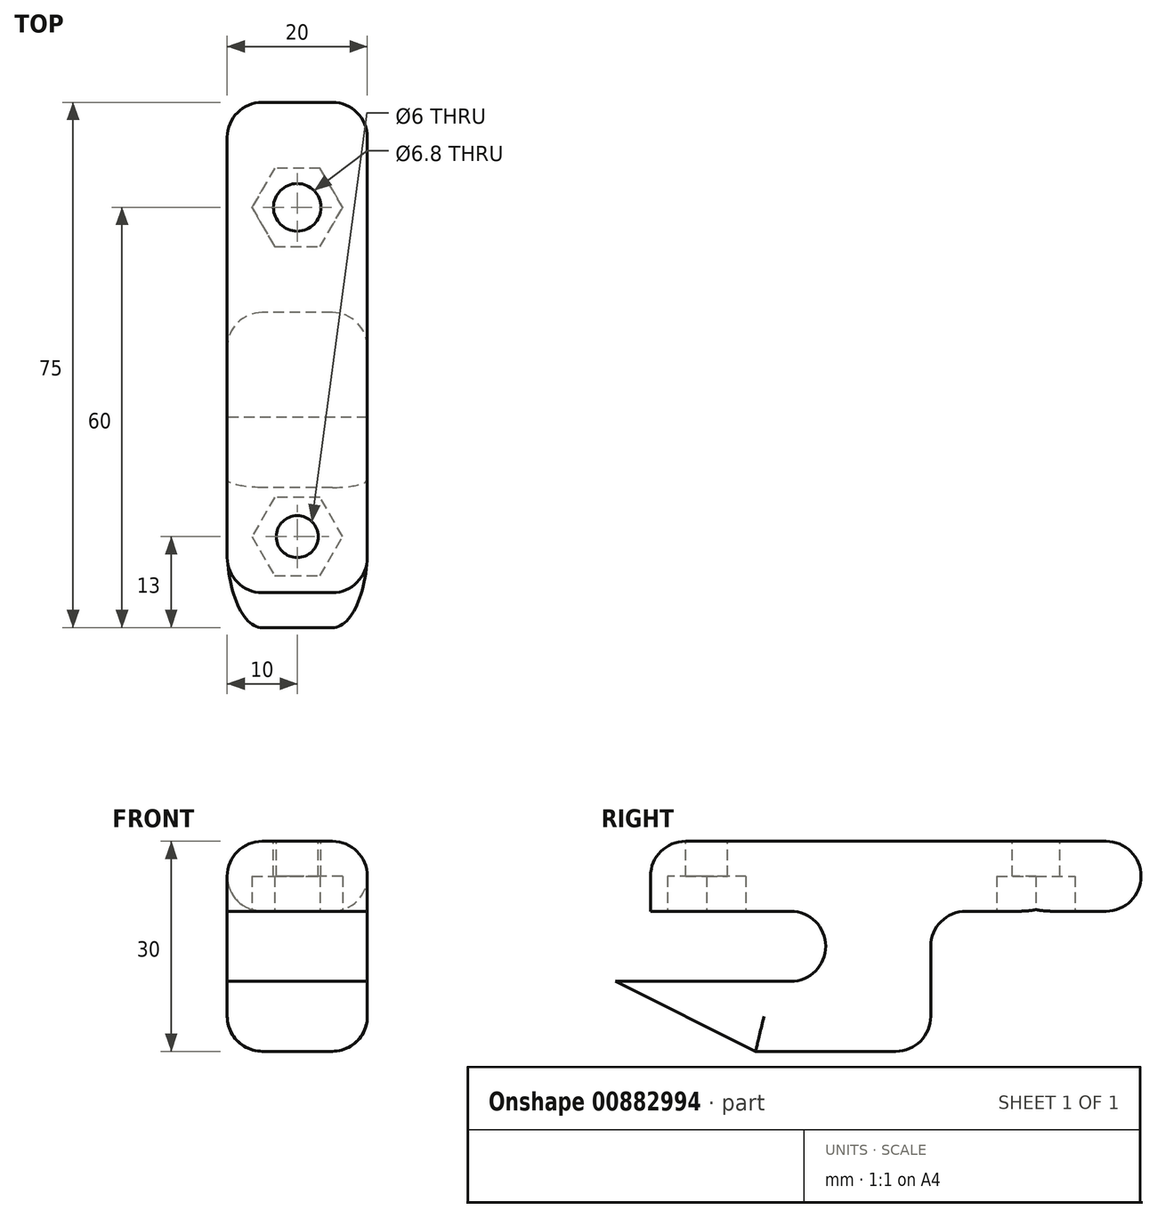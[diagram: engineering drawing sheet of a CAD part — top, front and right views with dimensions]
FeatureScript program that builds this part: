
annotation { "Feature Type Name" : "Feature", "Feature Type Description" : "" }
export const myFeature = defineFeature(function(context is Context, id is Id, definition is map)
    precondition{}
    {
        {
            var Q0;
            Q0=qCreatedBy(makeId("Right.planeOp"),FACE);
            var sketch = newSketch(context, id + "F0", { "sketchPlane" : qUnion([Q0])});
            skLineSegment(sketch, "E0.bottom", {"start": v(7.5, -5) * mm, "end": v(-7.5, -5) * mm});
            skLineSegment(sketch, "E0.top", {"start": v(7.5, 5) * mm, "end": v(-7.5, 5) * mm});
            skLineSegment(sketch, "E0.left", {"start": v(7.5, -5) * mm, "end": v(7.5, 5) * mm});
            skLineSegment(sketch, "E0.right", {"start": v(-7.5, -5) * mm, "end": v(-7.5, 5) * mm});
            skPoint(sketch, "E0.middle", {"position": v(0, 0) * mm});
            skLineSegment(sketch, "E1.bottom", {"start": v(7.5, 5) * mm, "end": v(-32.5, 5) * mm});
            skLineSegment(sketch, "E1.top", {"start": v(7.5, 15) * mm, "end": v(-32.5, 15) * mm});
            skLineSegment(sketch, "E1.left", {"start": v(7.5, 5) * mm, "end": v(7.5, 15) * mm});
            skLineSegment(sketch, "E1.right", {"start": v(-32.5, 5) * mm, "end": v(-32.5, 15) * mm});
            skLineSegment(sketch, "E2.bottom", {"start": v(7.5, -5) * mm, "end": v(-37.5, -5) * mm});
            skLineSegment(sketch, "E2.top", {"start": v(7.5, -15) * mm, "end": v(-37.5, -15) * mm});
            skLineSegment(sketch, "E2.left", {"start": v(7.5, -5) * mm, "end": v(7.5, -15) * mm});
            skLineSegment(sketch, "E2.right", {"start": v(-37.5, -5) * mm, "end": v(-37.5, -15) * mm});
            skLineSegment(sketch, "E3.bottom", {"start": v(7.5, 5) * mm, "end": v(37.5, 5) * mm});
            skLineSegment(sketch, "E3.top", {"start": v(7.5, 15) * mm, "end": v(37.5, 15) * mm});
            skLineSegment(sketch, "E3.right", {"start": v(37.5, 5) * mm, "end": v(37.5, 15) * mm});
            skSolve(sketch);
        }
        {
            var Q0;
            {var subQ0=makeQuery(id+"F0.imprint","IMPRINT",EDGE,{"derivedFrom":sQuery(id+"F0.wireOp",EDGE,"E1.left")});var subQ1=makeQuery(id+"F0.imprint","IMPRINT",EDGE,{"derivedFrom":sQuery(id+"F0.wireOp",EDGE,"E0.top")});var subQ2=makeQuery(id+"F0.imprint","IMPRINT",EDGE,{"derivedFrom":sQuery(id+"F0.wireOp",EDGE,"E0.bottom")});Q0=qUnion([makeQuery(id+"F0.imprint","IMPRINT",FACE,{"disambiguationData":[TD([[subQ2,1.0]])]}),makeQuery(id+"F0.imprint","IMPRINT",FACE,{"disambiguationData":[TD([[subQ0,-1.0]])]}),makeQuery(id+"F0.imprint","IMPRINT",FACE,{"disambiguationData":[TD([[subQ2,-1.0]])]}),makeQuery(id+"F0.imprint","IMPRINT",FACE,{"disambiguationData":[TD([[subQ1,-1.0]])]})]);}
            extrude(context, id + "F1", {"entities" : qUnion([Q0]), "depth" : 20 * mm, "offsetDistance" : 25 * mm});
        }
        {
            var Q0;
            Q0=makeQuery(id+"F1.opExtrude","SWEPT_FACE",FACE,{"disambiguationData":[OSD([sQuery(id+"F0.wireOp",EDGE,"E1.top"),sQuery(id+"F0.wireOp",EDGE,"E3.top")])]});
            var sketch = newSketch(context, id + "F2", { "sketchPlane" : qUnion([Q0])});
            skCircle(sketch, "E4", {"center": v(10, 22.5) * mm, "radius": 3.4 * mm});
            skCircle(sketch, "E5", {"center": v(10, -24.5) * mm, "radius": 3 * mm});
            skSolve(sketch);
        }
        {
            var Q0;
            Q0=makeQuery(id+"F2.imprint","IMPRINT",FACE,{"disambiguationData":[TD([[makeQuery(id+"F2.imprint","IMPRINT",EDGE,{"derivedFrom":sQuery(id+"F2.wireOp",EDGE,"E5")}),1.0]])]});
            var Q1;
            Q1=makeQuery(id+"F2.imprint","IMPRINT",FACE,{"disambiguationData":[TD([[makeQuery(id+"F2.imprint","IMPRINT",EDGE,{"derivedFrom":sQuery(id+"F2.wireOp",EDGE,"E4")}),1.0]])]});
            extrude(context, id + "F3", {"entities" : qUnion([Q0, Q1]), "operationType" : NewBodyOperationType.REMOVE, "endBound" : BoundingType.UP_TO_NEXT, "oppositeDirection" : true, "depth" : 25 * mm, "offsetDistance" : 25 * mm});
        }
        {
            var Q0;
            Q0=makeQuery(id+"F1.opExtrude","SWEPT_FACE",FACE,{"disambiguationData":[OSD([sQuery(id+"F0.wireOp",EDGE,"E3.bottom")])]});
            var sketch = newSketch(context, id + "F4", { "sketchPlane" : qUnion([Q0])});
            skCircle(sketch, "E6.cCircle", {"center": v(10, -22.5) * mm, "radius": 5.6 * mm, "construction": true});
            skLineSegment(sketch, "E6.0", {"start": v(13.23, -28.1) * mm, "end": v(6.77, -28.1) * mm});
            skLineSegment(sketch, "E6.1", {"start": v(6.77, -28.1) * mm, "end": v(3.53, -22.5) * mm});
            skLineSegment(sketch, "E6.2", {"start": v(3.53, -22.5) * mm, "end": v(6.77, -16.9) * mm});
            skLineSegment(sketch, "E6.3", {"start": v(6.77, -16.9) * mm, "end": v(13.23, -16.9) * mm});
            skLineSegment(sketch, "E6.4", {"start": v(13.23, -16.9) * mm, "end": v(16.47, -22.5) * mm});
            skLineSegment(sketch, "E6.5", {"start": v(16.47, -22.5) * mm, "end": v(13.23, -28.1) * mm});
            skPoint(sketch, "E6.0.midPoint", {"position": v(10, -28.1) * mm});
            skSolve(sketch);
        }
        {
            var Q0;
            Q0 = qSketchRegion(id + "F4", true);
            extrude(context, id + "F5", {"entities" : qUnion([Q0]), "operationType" : NewBodyOperationType.REMOVE, "oppositeDirection" : true, "depth" : 5 * mm, "offsetDistance" : 25 * mm});
        }
        {
            var Q0;
            Q0=makeQuery(id+"F1.opExtrude","SWEPT_EDGE",EDGE,{"disambiguationData":[OSD([sQuery(id+"F0.wireOp",EDGE,"E2.top"),sQuery(id+"F0.wireOp",EDGE,"E2.right")])]});
            chamfer(context, id + "F6", {"entities" : qUnion([Q0]), "chamferType" : ChamferType.TWO_OFFSETS, "width1" : 20 * mm, "oppositeDirection" : false, "width2" : 10 * mm, "tangentPropagation" : true});
        }
        {
            var Q0;
            Q0=makeQuery(id+"F1.opExtrude","CAP_EDGE",EDGE,{"disambiguationData":[OSD([sQuery(id+"F0.wireOp",EDGE,"E3.right")])],"isStart":true});
            var Q1;
            Q1=makeQuery(id+"F1.opExtrude","CAP_EDGE",EDGE,{"disambiguationData":[OSD([sQuery(id+"F0.wireOp",EDGE,"E3.right")])],"isStart":false});
            var Q2;
            Q2=makeQuery(id+"F1.opExtrude","CAP_EDGE",EDGE,{"disambiguationData":[OSD([sQuery(id+"F0.wireOp",EDGE,"E0.left"),sQuery(id+"F0.wireOp",EDGE,"E2.left")])],"isStart":false});
            var Q3;
            Q3=makeQuery(id+"F1.opExtrude","CAP_EDGE",EDGE,{"disambiguationData":[OSD([sQuery(id+"F0.wireOp",EDGE,"E0.left"),sQuery(id+"F0.wireOp",EDGE,"E2.left")])],"isStart":true});
            var Q4;
            Q4=makeQuery(id+"F1.opExtrude","SWEPT_EDGE",EDGE,{"disambiguationData":[OSD([sQuery(id+"F0.wireOp",EDGE,"E2.top"),sQuery(id+"F0.wireOp",EDGE,"E2.left")])]});
            var Q5;
            Q5=makeQuery(id+"F1.opExtrude","CAP_EDGE",EDGE,{"disambiguationData":[OSD([sQuery(id+"F0.wireOp",EDGE,"E2.top")])],"isStart":false});
            var Q6;
            Q6=makeQuery(id+"F1.opExtrude","CAP_EDGE",EDGE,{"disambiguationData":[OSD([sQuery(id+"F0.wireOp",EDGE,"E2.top")])],"isStart":true});
            var Q7;
            {var subQ0=sQuery(id+"F0.wireOp",EDGE,"E2.right");var subQ1=sQuery(id+"F0.wireOp",EDGE,"E2.top");Q7=makeQuery(id+"F6.opChamfer","BLEND_EDGE",EDGE,{"blendedFrom":[makeQuery(id+"F1.opExtrude","SWEPT_EDGE",EDGE,{"disambiguationData":[OSD([subQ1,subQ0])]}),makeQuery(id+"F1.opExtrude","CAP_FACE",FACE,{"disambiguationData":[OSD([sQuery(id+"F0.wireOp",EDGE,"E0.left"),sQuery(id+"F0.wireOp",EDGE,"E0.right"),sQuery(id+"F0.wireOp",EDGE,"E1.bottom"),sQuery(id+"F0.wireOp",EDGE,"E1.top"),sQuery(id+"F0.wireOp",EDGE,"E1.right"),sQuery(id+"F0.wireOp",EDGE,"E2.bottom"),subQ1,sQuery(id+"F0.wireOp",EDGE,"E2.left"),subQ0,sQuery(id+"F0.wireOp",EDGE,"E3.bottom"),sQuery(id+"F0.wireOp",EDGE,"E3.top"),sQuery(id+"F0.wireOp",EDGE,"E3.right")])],"isStart":true})],"blendedInto":[makeQuery(id+"F1.opExtrude","CAP_FACE",FACE,{"disambiguationData":[OSD([sQuery(id+"F0.wireOp",EDGE,"E0.left"),sQuery(id+"F0.wireOp",EDGE,"E0.right"),sQuery(id+"F0.wireOp",EDGE,"E1.bottom"),sQuery(id+"F0.wireOp",EDGE,"E1.top"),sQuery(id+"F0.wireOp",EDGE,"E1.right"),sQuery(id+"F0.wireOp",EDGE,"E2.bottom"),subQ1,sQuery(id+"F0.wireOp",EDGE,"E2.left"),subQ0,sQuery(id+"F0.wireOp",EDGE,"E3.bottom"),sQuery(id+"F0.wireOp",EDGE,"E3.top"),sQuery(id+"F0.wireOp",EDGE,"E3.right")])],"isStart":true})]});}
            var Q8;
            {var subQ0=sQuery(id+"F0.wireOp",EDGE,"E2.right");var subQ1=sQuery(id+"F0.wireOp",EDGE,"E2.top");Q8=makeQuery(id+"F6.opChamfer","BLEND_EDGE",EDGE,{"blendedFrom":[makeQuery(id+"F1.opExtrude","SWEPT_EDGE",EDGE,{"disambiguationData":[OSD([subQ1,subQ0])]}),makeQuery(id+"F1.opExtrude","CAP_FACE",FACE,{"disambiguationData":[OSD([sQuery(id+"F0.wireOp",EDGE,"E0.left"),sQuery(id+"F0.wireOp",EDGE,"E0.right"),sQuery(id+"F0.wireOp",EDGE,"E1.bottom"),sQuery(id+"F0.wireOp",EDGE,"E1.top"),sQuery(id+"F0.wireOp",EDGE,"E1.right"),sQuery(id+"F0.wireOp",EDGE,"E2.bottom"),subQ1,sQuery(id+"F0.wireOp",EDGE,"E2.left"),subQ0,sQuery(id+"F0.wireOp",EDGE,"E3.bottom"),sQuery(id+"F0.wireOp",EDGE,"E3.top"),sQuery(id+"F0.wireOp",EDGE,"E3.right")])],"isStart":false})],"blendedInto":[makeQuery(id+"F1.opExtrude","CAP_FACE",FACE,{"disambiguationData":[OSD([sQuery(id+"F0.wireOp",EDGE,"E0.left"),sQuery(id+"F0.wireOp",EDGE,"E0.right"),sQuery(id+"F0.wireOp",EDGE,"E1.bottom"),sQuery(id+"F0.wireOp",EDGE,"E1.top"),sQuery(id+"F0.wireOp",EDGE,"E1.right"),sQuery(id+"F0.wireOp",EDGE,"E2.bottom"),subQ1,sQuery(id+"F0.wireOp",EDGE,"E2.left"),subQ0,sQuery(id+"F0.wireOp",EDGE,"E3.bottom"),sQuery(id+"F0.wireOp",EDGE,"E3.top"),sQuery(id+"F0.wireOp",EDGE,"E3.right")])],"isStart":false})]});}
            var Q9;
            Q9=makeQuery(id+"F1.opExtrude","CAP_EDGE",EDGE,{"disambiguationData":[OSD([sQuery(id+"F0.wireOp",EDGE,"E3.bottom")])],"isStart":false});
            var Q10;
            Q10=makeQuery(id+"F1.opExtrude","CAP_EDGE",EDGE,{"disambiguationData":[OSD([sQuery(id+"F0.wireOp",EDGE,"E3.bottom")])],"isStart":true});
            var Q11;
            Q11=makeQuery(id+"F1.opExtrude","CAP_EDGE",EDGE,{"disambiguationData":[OSD([sQuery(id+"F0.wireOp",EDGE,"E1.top"),sQuery(id+"F0.wireOp",EDGE,"E3.top")])],"isStart":true});
            var Q12;
            Q12=makeQuery(id+"F1.opExtrude","CAP_EDGE",EDGE,{"disambiguationData":[OSD([sQuery(id+"F0.wireOp",EDGE,"E1.top"),sQuery(id+"F0.wireOp",EDGE,"E3.top")])],"isStart":false});
            var Q13;
            Q13=makeQuery(id+"F1.opExtrude","CAP_EDGE",EDGE,{"disambiguationData":[OSD([sQuery(id+"F0.wireOp",EDGE,"E1.right")])],"isStart":false});
            var Q14;
            Q14=makeQuery(id+"F1.opExtrude","CAP_EDGE",EDGE,{"disambiguationData":[OSD([sQuery(id+"F0.wireOp",EDGE,"E1.right")])],"isStart":true});
            var Q15;
            Q15=makeQuery(id+"F1.opExtrude","SWEPT_EDGE",EDGE,{"disambiguationData":[OSD([sQuery(id+"F0.wireOp",EDGE,"E1.top"),sQuery(id+"F0.wireOp",EDGE,"E1.right")])]});
            var Q16;
            Q16=makeQuery(id+"F1.opExtrude","SWEPT_EDGE",EDGE,{"disambiguationData":[OSD([sQuery(id+"F0.wireOp",EDGE,"E3.top"),sQuery(id+"F0.wireOp",EDGE,"E3.right")])]});
            var Q17;
            Q17=makeQuery(id+"F1.opExtrude","SWEPT_EDGE",EDGE,{"disambiguationData":[OSD([sQuery(id+"F0.wireOp",EDGE,"E3.bottom"),sQuery(id+"F0.wireOp",EDGE,"E3.right")])]});
            var Q18;
            Q18=makeQuery(id+"F1.opExtrude","SWEPT_EDGE",EDGE,{"disambiguationData":[OSD([sQuery(id+"F0.wireOp",EDGE,"E0.top"),sQuery(id+"F0.wireOp",EDGE,"E0.left"),sQuery(id+"F0.wireOp",EDGE,"E1.left"),sQuery(id+"F0.wireOp",EDGE,"E3.bottom")])]});
            var Q19;
            Q19=makeQuery(id+"F1.opExtrude","SWEPT_EDGE",EDGE,{"disambiguationData":[OSD([sQuery(id+"F0.wireOp",EDGE,"E0.bottom"),sQuery(id+"F0.wireOp",EDGE,"E0.right"),sQuery(id+"F0.wireOp",EDGE,"E2.bottom")])]});
            var Q20;
            Q20=makeQuery(id+"F1.opExtrude","SWEPT_EDGE",EDGE,{"disambiguationData":[OSD([sQuery(id+"F0.wireOp",EDGE,"E0.top"),sQuery(id+"F0.wireOp",EDGE,"E0.right"),sQuery(id+"F0.wireOp",EDGE,"E1.bottom")])]});
            fillet(context, id + "F7", {"entities" : qUnion([Q0, Q1, Q2, Q3, Q4, Q5, Q6, Q7, Q8, Q9, Q10, Q11, Q12, Q13, Q14, Q15, Q16, Q17, Q18, Q19, Q20]), "radius" : 5 * mm, "tangentPropagation" : true, "allowEdgeOverflow" : false});
        }
        {
            var Q0;
            Q0=makeQuery(id+"F1.opExtrude","SWEPT_FACE",FACE,{"disambiguationData":[OSD([sQuery(id+"F0.wireOp",EDGE,"E1.bottom")])]});
            var sketch = newSketch(context, id + "F8", { "sketchPlane" : qUnion([Q0])});
            skCircle(sketch, "E7.cCircle", {"center": v(10, 24.5) * mm, "radius": 5.6 * mm, "construction": true});
            skLineSegment(sketch, "E7.0", {"start": v(6.77, 30.1) * mm, "end": v(13.23, 30.1) * mm});
            skLineSegment(sketch, "E7.1", {"start": v(13.23, 30.1) * mm, "end": v(16.47, 24.5) * mm});
            skLineSegment(sketch, "E7.2", {"start": v(16.47, 24.5) * mm, "end": v(13.23, 18.9) * mm});
            skLineSegment(sketch, "E7.3", {"start": v(13.23, 18.9) * mm, "end": v(6.77, 18.9) * mm});
            skLineSegment(sketch, "E7.4", {"start": v(6.77, 18.9) * mm, "end": v(3.53, 24.5) * mm});
            skLineSegment(sketch, "E7.5", {"start": v(3.53, 24.5) * mm, "end": v(6.77, 30.1) * mm});
            skPoint(sketch, "E7.0.midPoint", {"position": v(10, 30.1) * mm});
            skSolve(sketch);
        }
        {
            var Q0;
            Q0 = qSketchRegion(id + "F8", true);
            extrude(context, id + "F9", {"entities" : qUnion([Q0]), "operationType" : NewBodyOperationType.REMOVE, "oppositeDirection" : true, "depth" : 5 * mm, "offsetDistance" : 25 * mm});
        }
    });
